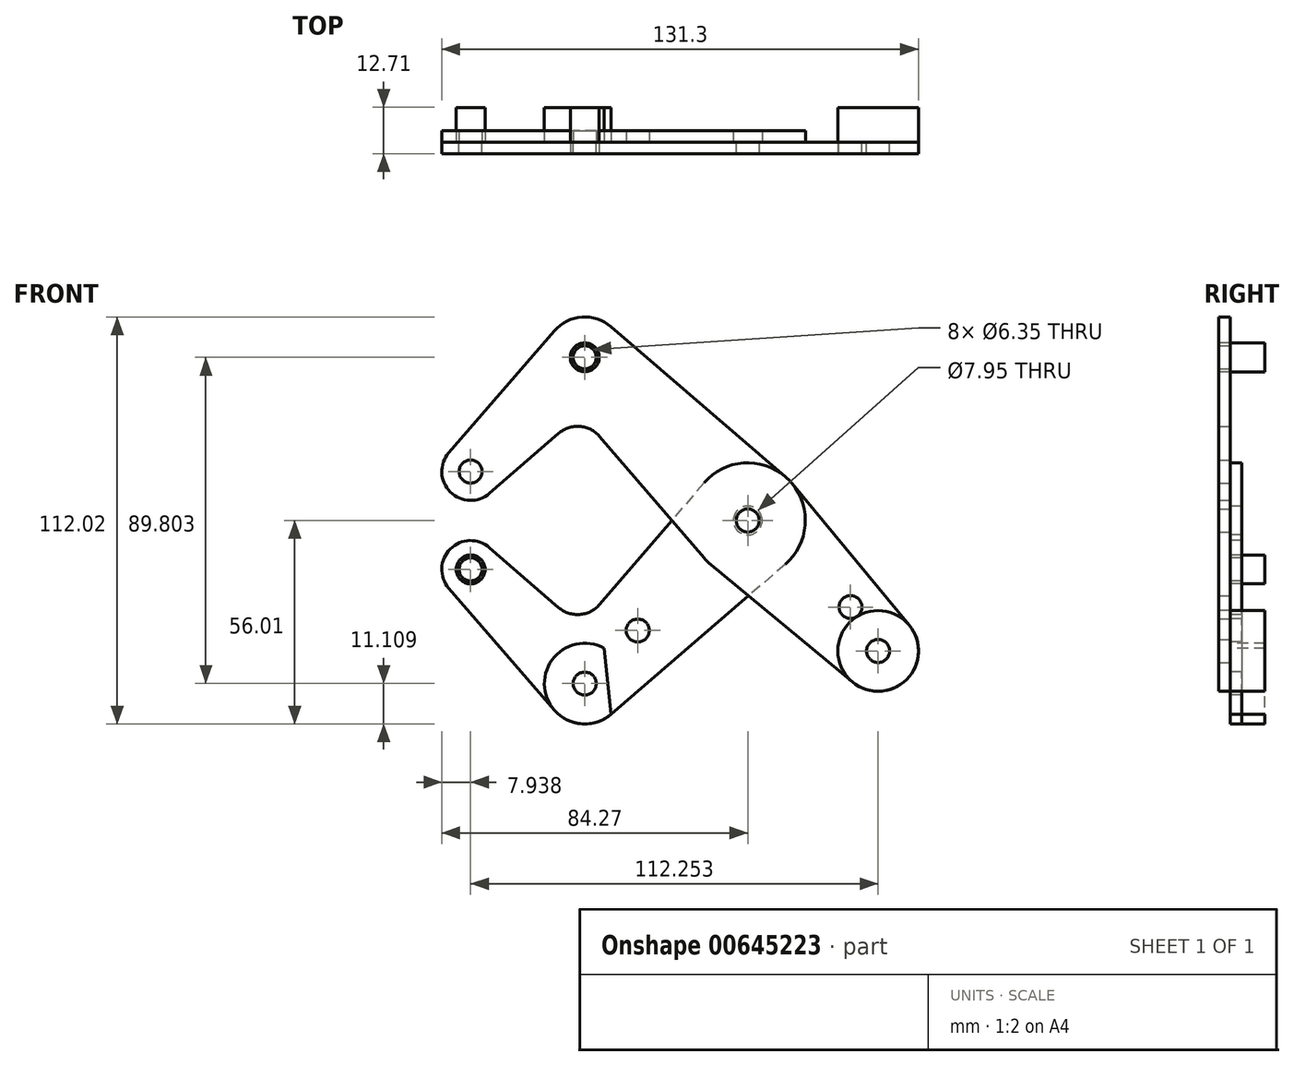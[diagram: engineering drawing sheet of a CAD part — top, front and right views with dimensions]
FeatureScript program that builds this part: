
annotation { "Feature Type Name" : "Feature", "Feature Type Description" : "" }
export const myFeature = defineFeature(function(context is Context, id is Id, definition is map)
    precondition{}
    {
        {
            var Q0;
            Q0=qCreatedBy(makeId("Front.planeOp"),FACE);
            var sketch = newSketch(context, id + "F0", { "sketchPlane" : qUnion([Q0])});
            skCircle(sketch, "E0", {"center": v(0, 0) * mm, "radius": 15.88 * mm});
            skCircle(sketch, "E1", {"center": v(0, 0) * mm, "radius": 3.98 * mm});
            skCircle(sketch, "E2", {"center": v(35.92, -35.92) * mm, "radius": 11.11 * mm});
            skCircle(sketch, "E3", {"center": v(35.92, -35.92) * mm, "radius": 3.18 * mm});
            skLineSegment(sketch, "E4", {"start": v(0, 0) * mm, "end": v(35.92, -35.92) * mm, "construction": true});
            skCircle(sketch, "E5", {"center": v(28.32, -23.83) * mm, "radius": 3.18 * mm});
            skCircle(sketch, "E6", {"center": v(0, 0) * mm, "radius": 3.18 * mm});
            skLineSegment(sketch, "E7", {"start": v(28.83, -44.48) * mm, "end": v(-10.12, -12.23) * mm});
            skLineSegment(sketch, "E8", {"start": v(12.23, 10.12) * mm, "end": v(44.48, -28.83) * mm});
            skCircle(sketch, "E9", {"center": v(-44.9, 44.9) * mm, "radius": 11.11 * mm});
            skCircle(sketch, "E10", {"center": v(-44.9, 44.9) * mm, "radius": 3.18 * mm});
            skLineSegment(sketch, "E11", {"start": v(-37.66, 53.33) * mm, "end": v(10.35, 12.04) * mm});
            skLineSegment(sketch, "E12", {"start": v(0, 0) * mm, "end": v(-44.9, 44.9) * mm, "construction": true});
            skCircle(sketch, "E13", {"center": v(-76.33, 13.47) * mm, "radius": 7.94 * mm});
            skCircle(sketch, "E14", {"center": v(-76.33, 13.47) * mm, "radius": 3.18 * mm});
            skLineSegment(sketch, "E15", {"start": v(-76.33, 13.47) * mm, "end": v(-44.9, 44.9) * mm, "construction": true});
            skLineSegment(sketch, "E16", {"start": v(-82.33, 18.67) * mm, "end": v(-53.3, 52.18) * mm});
            skCircle(sketch, "E17", {"center": v(-76.33, -13.47) * mm, "radius": 7.94 * mm});
            skCircle(sketch, "E18", {"center": v(-76.33, -13.47) * mm, "radius": 3.18 * mm});
            skCircle(sketch, "E19", {"center": v(-44.9, -44.9) * mm, "radius": 11.11 * mm});
            skCircle(sketch, "E20", {"center": v(-44.9, -44.9) * mm, "radius": 3.18 * mm});
            skLineSegment(sketch, "E21", {"start": v(-44.9, -44.9) * mm, "end": v(-76.33, -13.47) * mm, "construction": true});
            skLineSegment(sketch, "E22", {"start": v(-76.33, -13.47) * mm, "end": v(-76.33, 13.47) * mm, "construction": true});
            skLineSegment(sketch, "E23", {"start": v(-71.13, -7.47) * mm, "end": v(-52.08, -23.98) * mm});
            skLineSegment(sketch, "E24", {"start": v(10.35, -12.04) * mm, "end": v(-37.66, -53.33) * mm});
            skLineSegment(sketch, "E25", {"start": v(-12.04, 10.35) * mm, "end": v(-40.85, -23.15) * mm});
            skLineSegment(sketch, "E26", {"start": v(-82.33, -18.67) * mm, "end": v(-53.3, -52.18) * mm});
            skPoint(sketch, "E27.newPointA", {"position": v(-58.2, -43.33) * mm});
            skPoint(sketch, "E27.newPointB", {"position": v(-29.74, -43.33) * mm});
            skArc(sketch, "E27.filletArc", {"start": v(-52.08, -23.98) * mm, "mid": v(-46.3, -25.9) * mm, "end": v(-40.85, -23.15) * mm});
            skCircle(sketch, "E28", {"center": v(-30.3, -30.3) * mm, "radius": 3.18 * mm});
            skLineSegment(sketch, "E29", {"start": v(-12.04, -10.35) * mm, "end": v(-40.85, 23.15) * mm});
            skLineSegment(sketch, "E30", {"start": v(-71.13, 7.47) * mm, "end": v(-52.08, 23.98) * mm});
            skArc(sketch, "E31.filletArc", {"start": v(-40.85, 23.15) * mm, "mid": v(-46.3, 25.9) * mm, "end": v(-52.08, 23.98) * mm});
            skLineSegment(sketch, "E32", {"start": v(-44.9, -44.9) * mm, "end": v(0, 0) * mm, "construction": true});
            skSolve(sketch);
        }
        {
            var Q0;
            {var subQ0=sQuery(id+"F0.wireOp",EDGE,"E11");Q0=makeQuery(id+"F0.imprint","IMPRINT",FACE,{"disambiguationData":[TD([[makeQuery(id+"F0.imprint","IMPRINT",EDGE,{"derivedFrom":subQ0}),-1.0]])]});}
            var Q1;
            Q1=makeQuery(id+"F0.imprint","IMPRINT",FACE,{"disambiguationData":[TD([[makeQuery(id+"F0.imprint","IMPRINT",EDGE,{"derivedFrom":sQuery(id+"F0.wireOp",EDGE,"E14")}),-1.0]])]});
            var Q2;
            Q2=makeQuery(id+"F0.imprint","IMPRINT",FACE,{"disambiguationData":[TD([[makeQuery(id+"F0.imprint","IMPRINT",EDGE,{"derivedFrom":sQuery(id+"F0.wireOp",EDGE,"E10")}),-1.0]])]});
            var Q3;
            Q3=makeQuery(id+"F0.imprint","IMPRINT",FACE,{"disambiguationData":[TD([[makeQuery(id+"F0.imprint","IMPRINT",EDGE,{"derivedFrom":sQuery(id+"F0.wireOp",EDGE,"E1")}),-1.0]])]});
            var Q4;
            {var subQ0=sQuery(id+"F0.wireOp",EDGE,"E7");var subQ1=sQuery(id+"F0.wireOp",EDGE,"E0");var subQ2=makeQuery(id+"F0.imprint","INTERSECT",VERTEX,{"derivedFrom":[subQ1,subQ0]});Q4=makeQuery(id+"F0.imprint","IMPRINT",FACE,{"disambiguationData":[TD([[makeQuery(id+"F0.imprint","IMPRINT",EDGE,{"disambiguationData":[TD([[subQ2,-1.0]])],"derivedFrom":subQ1}),-1.0]])]});}
            var Q5;
            {var subQ0=sQuery(id+"F0.wireOp",EDGE,"E25");var subQ1=sQuery(id+"F0.wireOp",EDGE,"E0");var subQ2=makeQuery(id+"F0.imprint","INTERSECT",VERTEX,{"derivedFrom":[subQ1,subQ0]});Q5=makeQuery(id+"F0.imprint","IMPRINT",FACE,{"disambiguationData":[TD([[makeQuery(id+"F0.imprint","IMPRINT",EDGE,{"disambiguationData":[TD([[subQ2,-1.0]])],"derivedFrom":subQ1}),-1.0]])]});}
            var Q6;
            {var subQ0=sQuery(id+"F0.wireOp",EDGE,"E5");Q6=makeQuery(id+"F0.imprint","IMPRINT",FACE,{"disambiguationData":[TD([[makeQuery(id+"F0.imprint","IMPRINT",EDGE,{"derivedFrom":subQ0}),-1.0]])]});}
            var Q7;
            Q7=makeQuery(id+"F0.imprint","IMPRINT",FACE,{"disambiguationData":[TD([[makeQuery(id+"F0.imprint","IMPRINT",EDGE,{"derivedFrom":sQuery(id+"F0.wireOp",EDGE,"E3")}),-1.0]])]});
            var Q8;
            Q8=makeQuery(id+"F0.imprint","IMPRINT",FACE,{"disambiguationData":[TD([[makeQuery(id+"F0.imprint","IMPRINT",EDGE,{"derivedFrom":sQuery(id+"F0.wireOp",EDGE,"E1")}),1.0]])]});
            extrude(context, id + "F1", {"entities" : qUnion([Q0, Q1, Q2, Q3, Q4, Q5, Q6, Q7, Q8]), "depth" : 3.17 * mm, "offsetDistance" : 25.4 * mm});
        }
        {
            var Q0;
            {var subQ12=sQuery(id+"F0.wireOp",EDGE,"E23");Q0=makeQuery(id+"F0.imprint","IMPRINT",FACE,{"disambiguationData":[TD([[makeQuery(id+"F0.imprint","IMPRINT",EDGE,{"derivedFrom":subQ12}),-1.0]])]});}
            var Q1;
            Q1=makeQuery(id+"F0.imprint","IMPRINT",FACE,{"disambiguationData":[TD([[makeQuery(id+"F0.imprint","IMPRINT",EDGE,{"derivedFrom":sQuery(id+"F0.wireOp",EDGE,"E20")}),-1.0]])]});
            var Q2;
            Q2=makeQuery(id+"F0.imprint","IMPRINT",FACE,{"disambiguationData":[TD([[makeQuery(id+"F0.imprint","IMPRINT",EDGE,{"derivedFrom":sQuery(id+"F0.wireOp",EDGE,"E18")}),-1.0]])]});
            var Q3;
            {var subQ0=sQuery(id+"F0.wireOp",EDGE,"E25");var subQ1=sQuery(id+"F0.wireOp",EDGE,"E0");var subQ2=makeQuery(id+"F0.imprint","INTERSECT",VERTEX,{"derivedFrom":[subQ1,subQ0]});Q3=makeQuery(id+"F0.imprint","IMPRINT",FACE,{"disambiguationData":[TD([[makeQuery(id+"F0.imprint","IMPRINT",EDGE,{"disambiguationData":[TD([[subQ2,-1.0]])],"derivedFrom":subQ1}),-1.0]])]});}
            var Q4;
            {var subQ0=sQuery(id+"F0.wireOp",EDGE,"E7");var subQ1=sQuery(id+"F0.wireOp",EDGE,"E0");var subQ2=makeQuery(id+"F0.imprint","INTERSECT",VERTEX,{"derivedFrom":[subQ1,subQ0]});Q4=makeQuery(id+"F0.imprint","IMPRINT",FACE,{"disambiguationData":[TD([[makeQuery(id+"F0.imprint","IMPRINT",EDGE,{"disambiguationData":[TD([[subQ2,-1.0]])],"derivedFrom":subQ1}),-1.0]])]});}
            var Q5;
            Q5=makeQuery(id+"F0.imprint","IMPRINT",FACE,{"disambiguationData":[TD([[makeQuery(id+"F0.imprint","IMPRINT",EDGE,{"derivedFrom":sQuery(id+"F0.wireOp",EDGE,"E1")}),-1.0]])]});
            extrude(context, id + "F2", {"entities" : qUnion([Q0, Q1, Q2, Q3, Q4, Q5]), "oppositeDirection" : true, "depth" : 3.17 * mm, "offsetDistance" : 25.4 * mm});
        }
        {
            var Q0;
            Q0=makeQuery(id+"F1.opExtrude","CAP_FACE",FACE,{"disambiguationData":[OSD([sQuery(id+"F0.wireOp",EDGE,"E0"),sQuery(id+"F0.wireOp",EDGE,"E2"),sQuery(id+"F0.wireOp",EDGE,"E3"),sQuery(id+"F0.wireOp",EDGE,"E5"),sQuery(id+"F0.wireOp",EDGE,"E6"),sQuery(id+"F0.wireOp",EDGE,"E7"),sQuery(id+"F0.wireOp",EDGE,"E8"),sQuery(id+"F0.wireOp",EDGE,"E9"),sQuery(id+"F0.wireOp",EDGE,"E10"),sQuery(id+"F0.wireOp",EDGE,"E11"),sQuery(id+"F0.wireOp",EDGE,"E13"),sQuery(id+"F0.wireOp",EDGE,"E14"),sQuery(id+"F0.wireOp",EDGE,"E16"),sQuery(id+"F0.wireOp",EDGE,"E29"),sQuery(id+"F0.wireOp",EDGE,"E30"),sQuery(id+"F0.wireOp",EDGE,"E31.filletArc")])],"isStart":false});
            var sketch = newSketch(context, id + "F3", { "sketchPlane" : qUnion([Q0])});
            skCircle(sketch, "E33", {"center": v(-44.9, 44.9) * mm, "radius": 3.98 * mm});
            skCircle(sketch, "E34", {"center": v(0, 0) * mm, "radius": 3.98 * mm});
            skCircle(sketch, "E35", {"center": v(35.92, -35.92) * mm, "radius": 11.11 * mm});
            skSolve(sketch);
        }
        {
            var Q0;
            Q0=makeQuery(id+"F2.opExtrude","CAP_FACE",FACE,{"disambiguationData":[OSD([sQuery(id+"F0.wireOp",EDGE,"E0"),sQuery(id+"F0.wireOp",EDGE,"E1"),sQuery(id+"F0.wireOp",EDGE,"E17"),sQuery(id+"F0.wireOp",EDGE,"E18"),sQuery(id+"F0.wireOp",EDGE,"E19"),sQuery(id+"F0.wireOp",EDGE,"E20"),sQuery(id+"F0.wireOp",EDGE,"E23"),sQuery(id+"F0.wireOp",EDGE,"E24"),sQuery(id+"F0.wireOp",EDGE,"E25"),sQuery(id+"F0.wireOp",EDGE,"E26"),sQuery(id+"F0.wireOp",EDGE,"E27.filletArc"),sQuery(id+"F0.wireOp",EDGE,"E28")])],"isStart":true});
            var sketch = newSketch(context, id + "F4", { "sketchPlane" : qUnion([Q0])});
            skCircle(sketch, "E36", {"center": v(-44.9, -44.9) * mm, "radius": 11.11 * mm});
            skCircle(sketch, "E37", {"center": v(-76.33, -13.47) * mm, "radius": 3.98 * mm});
            skLineSegment(sketch, "E38", {"start": v(-39.51, -35.18) * mm, "end": v(-37.66, -53.33) * mm});
            skCircle(sketch, "E39.0", {"center": v(35.92, -35.92) * mm, "radius": 3.18 * mm, "construction": true});
            skLineSegment(sketch, "E40", {"start": v(35.92, -35.92) * mm, "end": v(-38.58, -43.55) * mm, "construction": true});
            skPoint(sketch, "E40.endSnap0", {"position": v(-38.58, -44.25) * mm});
            skSolve(sketch);
        }
        {
            var Q0;
            Q0=makeQuery(id+"F1.opExtrude","CAP_FACE",FACE,{"disambiguationData":[OSD([sQuery(id+"F0.wireOp",EDGE,"E0"),sQuery(id+"F0.wireOp",EDGE,"E2"),sQuery(id+"F0.wireOp",EDGE,"E3"),sQuery(id+"F0.wireOp",EDGE,"E5"),sQuery(id+"F0.wireOp",EDGE,"E6"),sQuery(id+"F0.wireOp",EDGE,"E7"),sQuery(id+"F0.wireOp",EDGE,"E8"),sQuery(id+"F0.wireOp",EDGE,"E9"),sQuery(id+"F0.wireOp",EDGE,"E10"),sQuery(id+"F0.wireOp",EDGE,"E11"),sQuery(id+"F0.wireOp",EDGE,"E13"),sQuery(id+"F0.wireOp",EDGE,"E14"),sQuery(id+"F0.wireOp",EDGE,"E16"),sQuery(id+"F0.wireOp",EDGE,"E29"),sQuery(id+"F0.wireOp",EDGE,"E30"),sQuery(id+"F0.wireOp",EDGE,"E31.filletArc")])],"isStart":true});
            cPlane(context, id + "F5", {"entities" : qUnion([Q0]), "cplaneType" : CPlaneType.OFFSET, "offset" : 9.52 * mm, "width" : 152.4 * mm, "height" : 152.4 * mm});
        }
        {
            var Q0;
            {var subQ2=sQuery(id+"F4.wireOp",EDGE,"E38");Q0=makeQuery(id+"F4.imprint","IMPRINT",FACE,{"disambiguationData":[TD([[makeQuery(id+"F4.imprint","IMPRINT",EDGE,{"derivedFrom":subQ2}),-1.0]])]});}
            var Q1;
            Q1=makeQuery(id+"F3.imprint","IMPRINT",FACE,{"disambiguationData":[TD([[makeQuery(id+"F3.imprint","IMPRINT",EDGE,{"derivedFrom":makeQuery(id+"F1.opExtrude","CAP_EDGE",EDGE,{"disambiguationData":[OSD([sQuery(id+"F0.wireOp",EDGE,"E3")])],"isStart":false})}),-1.0]])]});
            var Q2;
            Q2=makeQuery(id+"F4.imprint","IMPRINT",FACE,{"disambiguationData":[TD([[makeQuery(id+"F4.imprint","IMPRINT",EDGE,{"derivedFrom":sQuery(id+"F4.wireOp",EDGE,"E37")}),1.0]])]});
            var Q3;
            Q3=makeQuery(id+"F3.imprint","IMPRINT",FACE,{"disambiguationData":[TD([[makeQuery(id+"F3.imprint","IMPRINT",EDGE,{"derivedFrom":sQuery(id+"F3.wireOp",EDGE,"E33")}),1.0]])]});
            var Q4;
            Q4=makeQuery(id+"F3.imprint","IMPRINT",FACE,{"disambiguationData":[TD([[makeQuery(id+"F3.imprint","IMPRINT",EDGE,{"derivedFrom":makeQuery(id+"F1.opExtrude","CAP_EDGE",EDGE,{"disambiguationData":[OSD([sQuery(id+"F0.wireOp",EDGE,"E10")])],"isStart":false})}),1.0]])]});
            var Q5;
            Q5=makeQuery(id+"F4.imprint","IMPRINT",FACE,{"disambiguationData":[TD([[makeQuery(id+"F4.imprint","IMPRINT",EDGE,{"derivedFrom":makeQuery(id+"F2.opExtrude","CAP_EDGE",EDGE,{"disambiguationData":[OSD([sQuery(id+"F0.wireOp",EDGE,"E18")])],"isStart":true})}),1.0]])]});
            var Q6;
            Q6=makeQuery(id+"F4.imprint","IMPRINT",FACE,{"disambiguationData":[TD([[makeQuery(id+"F4.imprint","IMPRINT",EDGE,{"derivedFrom":makeQuery(id+"F2.opExtrude","CAP_EDGE",EDGE,{"disambiguationData":[OSD([sQuery(id+"F0.wireOp",EDGE,"E20")])],"isStart":true})}),1.0]])]});
            var Q7;
            Q7=makeQuery(id+"F3.imprint","IMPRINT",FACE,{"disambiguationData":[TD([[makeQuery(id+"F3.imprint","IMPRINT",EDGE,{"derivedFrom":makeQuery(id+"F1.opExtrude","CAP_EDGE",EDGE,{"disambiguationData":[OSD([sQuery(id+"F0.wireOp",EDGE,"E3")])],"isStart":false})}),1.0]])]});
            var Q8;
            Q8=qCreatedBy(id+"F5.planeOp",FACE);
            extrude(context, id + "F6", {"entities" : qUnion([Q0, Q1, Q2, Q3, Q4, Q5, Q6, Q7]), "endBound" : BoundingType.UP_TO_SURFACE, "oppositeDirection" : true, "depth" : 25.4 * mm, "endBoundEntityFace" : qUnion([Q8]), "offsetDistance" : 25.4 * mm});
        }
    });
